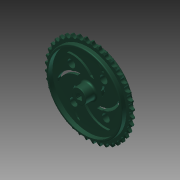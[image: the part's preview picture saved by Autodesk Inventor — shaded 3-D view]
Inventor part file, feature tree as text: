
AUTODESK INVENTOR PART (.ipt)
format: ipt  version: 2013 (Build 170138000, 138)  size: 3,381,248 bytes
history: native  units: mm (DEFAULTED — no unit token found)
features: imported_body x1, sketch x1, other x1, extrude x1
ambient origin geometry x8: Origin, YZ Plane, XZ Plane, XY Plane, X Axis, Y Axis, Z Axis, Center Point
bodies: Solid1 (feature_tree)
feature tree (4):
  imported_body  "Base1"
  sketch  "Sketch1"  dims[d1=2.2606mm d5=25.4mm d6=0.0mm d7=0.0mm d8=0.0mm]
  other  "Srf1"
  extrude  "ExtrusionSrf1"  Depth=25.4mm TaperAngle=0.0deg
